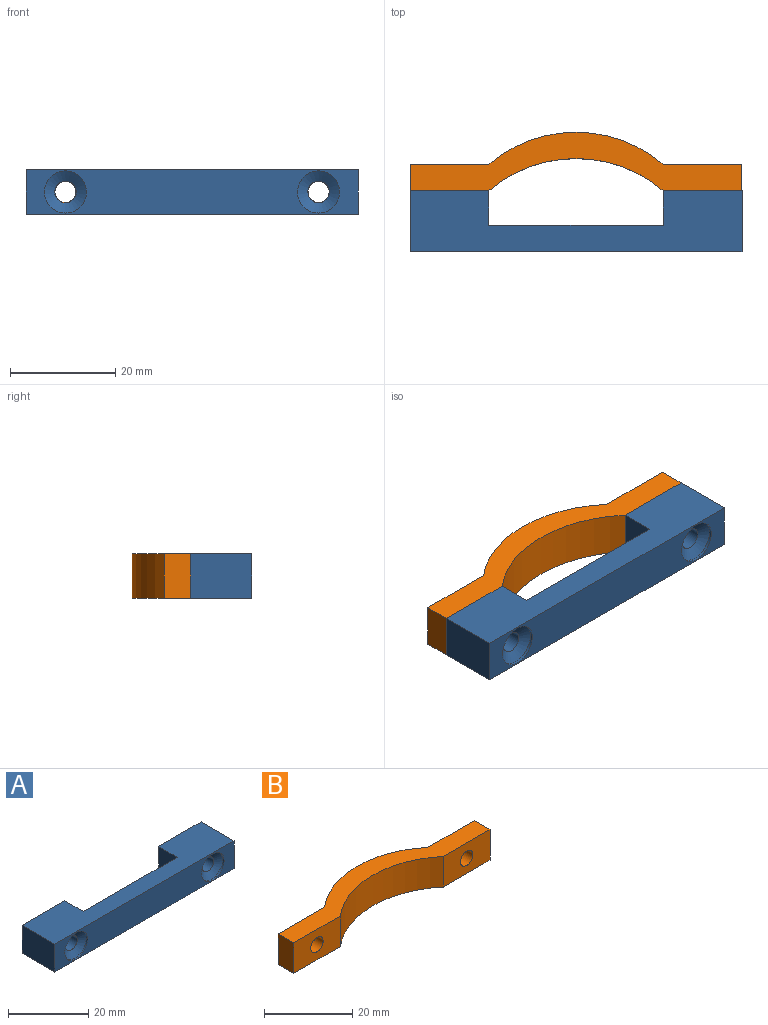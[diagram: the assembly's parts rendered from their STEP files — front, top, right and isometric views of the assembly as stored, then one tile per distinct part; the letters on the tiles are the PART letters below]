
ASSEMBLY  parts=2 mates=1
PART A: 16 faces, bbox 63.1x11.6x8.5 mm
  f0: cylinder r=2.05mm len=9.93mm, axis (0,-1,0), area 127.9mm2, adj f5,f14
  f1: cylinder r=2.05mm len=9.93mm, axis (0,-1,0), area 127.9mm2, adj f9,f12
  f2: plane 11.6x8.5mm, normal (-1,0,0), area 98.6mm2, adj f3,f9,f10,f11
  f3: plane 63.1x8.5mm, normal (0,-1,0), area 435.8mm2, adj f2,f4,f10,f11,f13,f15
  f4: plane 11.6x8.5mm, normal (1,0,0), area 98.6mm2, adj f3,f5,f10,f11
  f5: plane 15x8.5mm, normal (0,1,0), area 114.3mm2, adj f0,f4,f6,f10,f11
  f6: plane 8.5x6.6mm, normal (-1,0,0), area 56.1mm2, adj f5,f7,f10,f11
  f7: plane 33.1x8.5mm, normal (0,1,0), area 281.4mm2, adj f6,f8,f10,f11
  f8: plane 8.5x6.6mm, normal (1,0,0), area 56.1mm2, adj f7,f9,f10,f11
  f9: plane 15x8.5mm, normal (0,1,0), area 114.3mm2, adj f1,f2,f8,f10,f11
  f10: plane 63.1x11.6mm, normal (0,0,1), area 513.5mm2, adj f2,f3,f4,f5,f6,f7,f8,f9
  f11: plane 63.1x11.6mm, normal (0,0,-1), area 513.5mm2, adj f2,f3,f4,f5,f6,f7,f8,f9
  f12: cone r=0mm half-angle=59deg, axis (0,-1,0), area 43.2mm2, adj f1,f13
  f13: cylinder r=4mm len=8mm, axis (0,-1,0), area 12.6mm2, adj f3,f12
  f14: cone r=0mm half-angle=59deg, axis (0,-1,0), area 43.2mm2, adj f0,f15
  f15: cylinder r=4mm len=8mm, axis (0,-1,0), area 12.6mm2, adj f3,f14
PART B: 16 faces, bbox 63.1x11.1x8.5 mm
  f0: cone r=0mm half-angle=59deg, axis (0,1,0), area 44mm2, adj f13,f15
  f1: cone r=0mm half-angle=59deg, axis (0,1,0), area 44mm2, adj f12,f14
  f2: cylinder r=25.5mm len=33.1mm, axis (0,0,-1), area 306.2mm2, adj f3,f9,f10,f11
  f3: plane 15x8.5mm, normal (0,-1,0), area 114.9mm2, adj f2,f4,f10,f11,f14
  f4: plane 8.5x5mm, normal (1,0,0), area 42.5mm2, adj f3,f5,f10,f11
  f5: plane 15x8.5mm, normal (0,1,0), area 77.2mm2, adj f4,f6,f10,f11,f12
  f6: cylinder r=25.5mm len=33.1mm, axis (0,0,-1), area 306.2mm2, adj f5,f7,f10,f11
  f7: plane 15x8.5mm, normal (0,1,0), area 77.2mm2, adj f6,f8,f10,f11,f13
  f8: plane 8.5x5mm, normal (-1,0,0), area 42.5mm2, adj f7,f9,f10,f11
  f9: plane 15x8.5mm, normal (0,-1,0), area 114.9mm2, adj f2,f8,f10,f11,f15
  f10: plane 63.1x11.1mm, normal (0,0,1), area 315.5mm2, adj f2,f3,f4,f5,f6,f7,f8,f9
  f11: plane 63.1x11.1mm, normal (0,0,-1), area 315.5mm2, adj f2,f3,f4,f5,f6,f7,f8,f9
  f12: cylinder r=4mm len=8mm, axis (0,1,0), area 12.6mm2, adj f1,f5
  f13: cylinder r=4mm len=8mm, axis (0,1,0), area 12.6mm2, adj f0,f7
  f14: cylinder r=2mm len=4mm, axis (0,1,0), area 41.4mm2, adj f1,f3
  f15: cylinder r=2mm len=4mm, axis (0,1,0), area 41.4mm2, adj f0,f9
PLACE A t=(-1.99,-0.79,0)mm
PLACE B at identity
MATE fastened A.f0 <-> B.f1  axis (0,-1,0) through (31.76,11.33,4.25)mm
